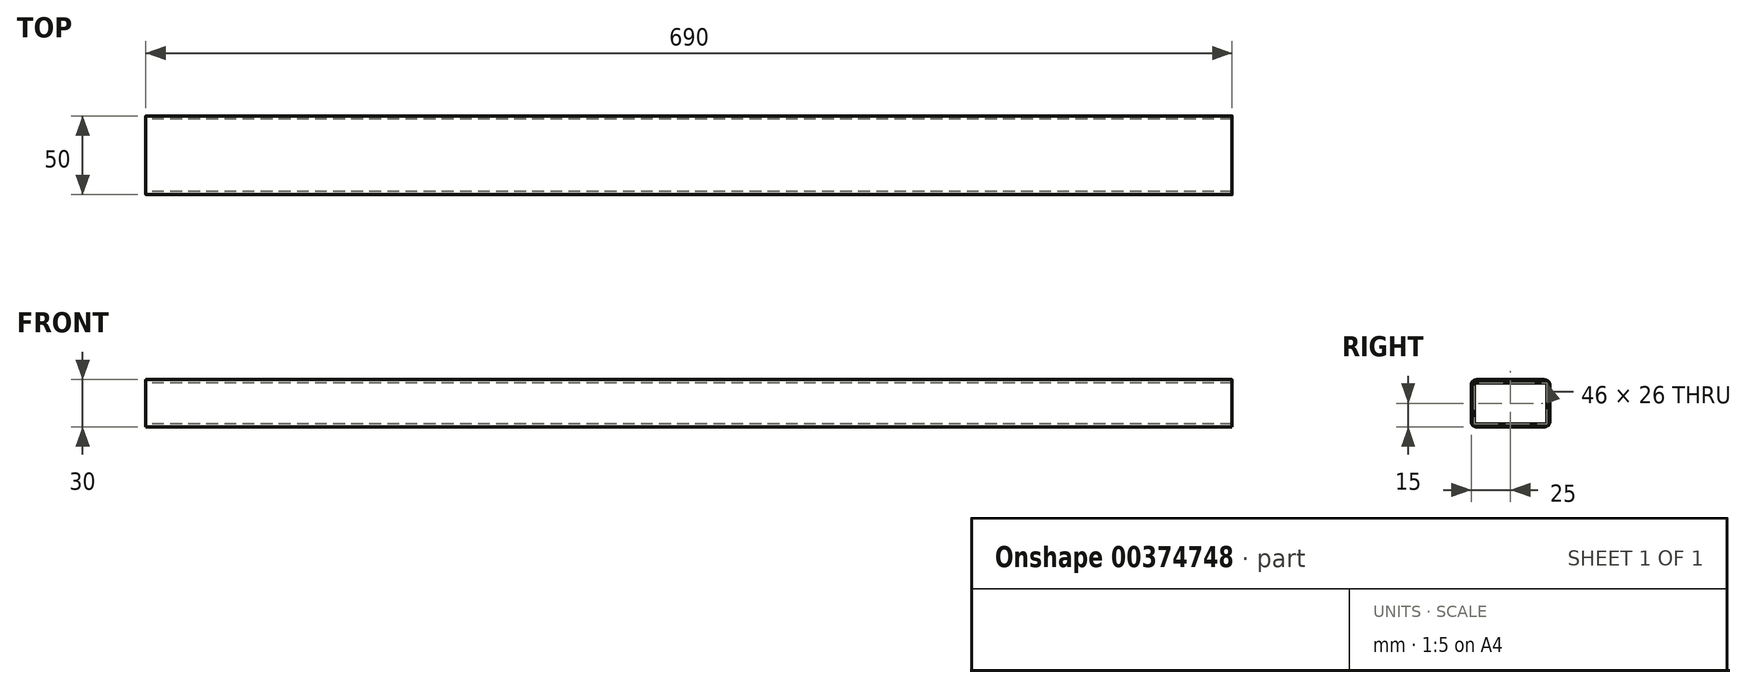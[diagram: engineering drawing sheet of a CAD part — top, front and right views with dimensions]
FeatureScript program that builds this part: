
annotation { "Feature Type Name" : "Feature", "Feature Type Description" : "" }
export const myFeature = defineFeature(function(context is Context, id is Id, definition is map)
    precondition{}
    {
        {
            var Q0;
            Q0=qCreatedBy(makeId("Right.planeOp"),FACE);
            var sketch = newSketch(context, id + "F0", { "sketchPlane" : qUnion([Q0])});
            skLineSegment(sketch, "E0.bottom", {"start": v(21.5, 15) * mm, "end": v(-21.5, 15) * mm});
            skLineSegment(sketch, "E0.top", {"start": v(21.5, -15) * mm, "end": v(-21.5, -15) * mm});
            skLineSegment(sketch, "E0.left", {"start": v(25, 11.5) * mm, "end": v(25, -11.5) * mm});
            skLineSegment(sketch, "E0.right", {"start": v(-25, 11.5) * mm, "end": v(-25, -11.5) * mm});
            skPoint(sketch, "E0.middle", {"position": v(0, 0) * mm});
            skLineSegment(sketch, "E1.bottom", {"start": v(23, 13) * mm, "end": v(-23, 13) * mm});
            skLineSegment(sketch, "E1.top", {"start": v(23, -13) * mm, "end": v(-23, -13) * mm});
            skLineSegment(sketch, "E1.left", {"start": v(23, 13) * mm, "end": v(23, -13) * mm});
            skLineSegment(sketch, "E1.right", {"start": v(-23, 13) * mm, "end": v(-23, -13) * mm});
            skPoint(sketch, "E2.visualSharp", {"position": v(-25, 15) * mm});
            skArc(sketch, "E2.filletArc", {"start": v(-21.5, 15) * mm, "mid": v(-23.97, 13.97) * mm, "end": v(-25, 11.5) * mm});
            skPoint(sketch, "E3.visualSharp", {"position": v(25, 15) * mm});
            skArc(sketch, "E3.filletArc", {"start": v(25, 11.5) * mm, "mid": v(23.97, 13.97) * mm, "end": v(21.5, 15) * mm});
            skPoint(sketch, "E4.visualSharp", {"position": v(25, -15) * mm});
            skArc(sketch, "E4.filletArc", {"start": v(21.5, -15) * mm, "mid": v(23.97, -13.97) * mm, "end": v(25, -11.5) * mm});
            skPoint(sketch, "E5.visualSharp", {"position": v(-25, -15) * mm});
            skArc(sketch, "E5.filletArc", {"start": v(-25, -11.5) * mm, "mid": v(-23.97, -13.97) * mm, "end": v(-21.5, -15) * mm});
            skSolve(sketch);
        }
        {
            var Q0;
            Q0=makeQuery(id+"F0.imprint","IMPRINT",FACE,{"disambiguationData":[TD([[makeQuery(id+"F0.imprint","IMPRINT",EDGE,{"derivedFrom":sQuery(id+"F0.wireOp",EDGE,"E0.bottom")}),1.0]])]});
            extrude(context, id + "F1", {"entities" : qUnion([Q0]), "depth" : 690 * mm});
        }
    });
